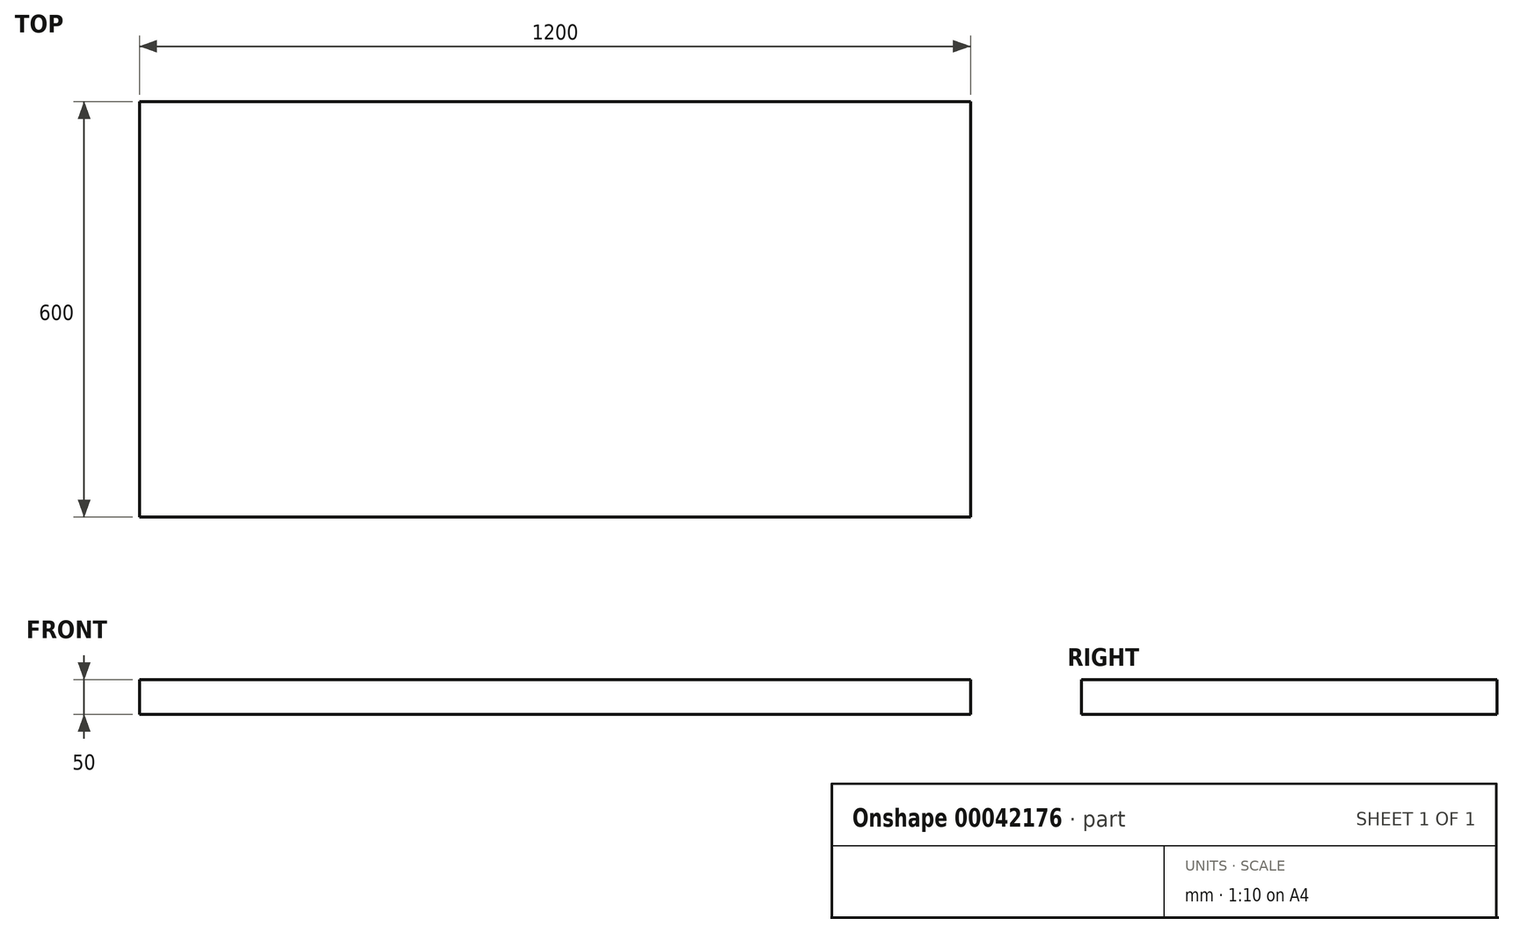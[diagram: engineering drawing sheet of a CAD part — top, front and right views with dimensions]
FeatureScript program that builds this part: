
annotation { "Feature Type Name" : "Feature", "Feature Type Description" : "" }
export const myFeature = defineFeature(function(context is Context, id is Id, definition is map)
    precondition{}
    {
        {
            var Q0;
            Q0=qCreatedBy(makeId("Top.planeOp"),FACE);
            var sketch = newSketch(context, id + "F0", { "sketchPlane" : qUnion([Q0])});
            skLineSegment(sketch, "E0.bottom", {"start": v(0, 0) * mm, "end": v(1200, 0) * mm});
            skLineSegment(sketch, "E0.top", {"start": v(0, 600) * mm, "end": v(1200, 600) * mm});
            skLineSegment(sketch, "E0.left", {"start": v(0, 0) * mm, "end": v(0, 600) * mm});
            skLineSegment(sketch, "E0.right", {"start": v(1200, 0) * mm, "end": v(1200, 600) * mm});
            skSolve(sketch);
        }
        {
            var Q0;
            Q0=makeQuery(id+"F0.imprint","IMPRINT",FACE,{"disambiguationData":[TD([[makeQuery(id+"F0.imprint","IMPRINT",EDGE,{"derivedFrom":sQuery(id+"F0.wireOp",EDGE,"E0.bottom")}),1.0]])]});
            extrude(context, id + "F1", {"entities" : qUnion([Q0]), "depth" : 50 * mm});
        }
    });
